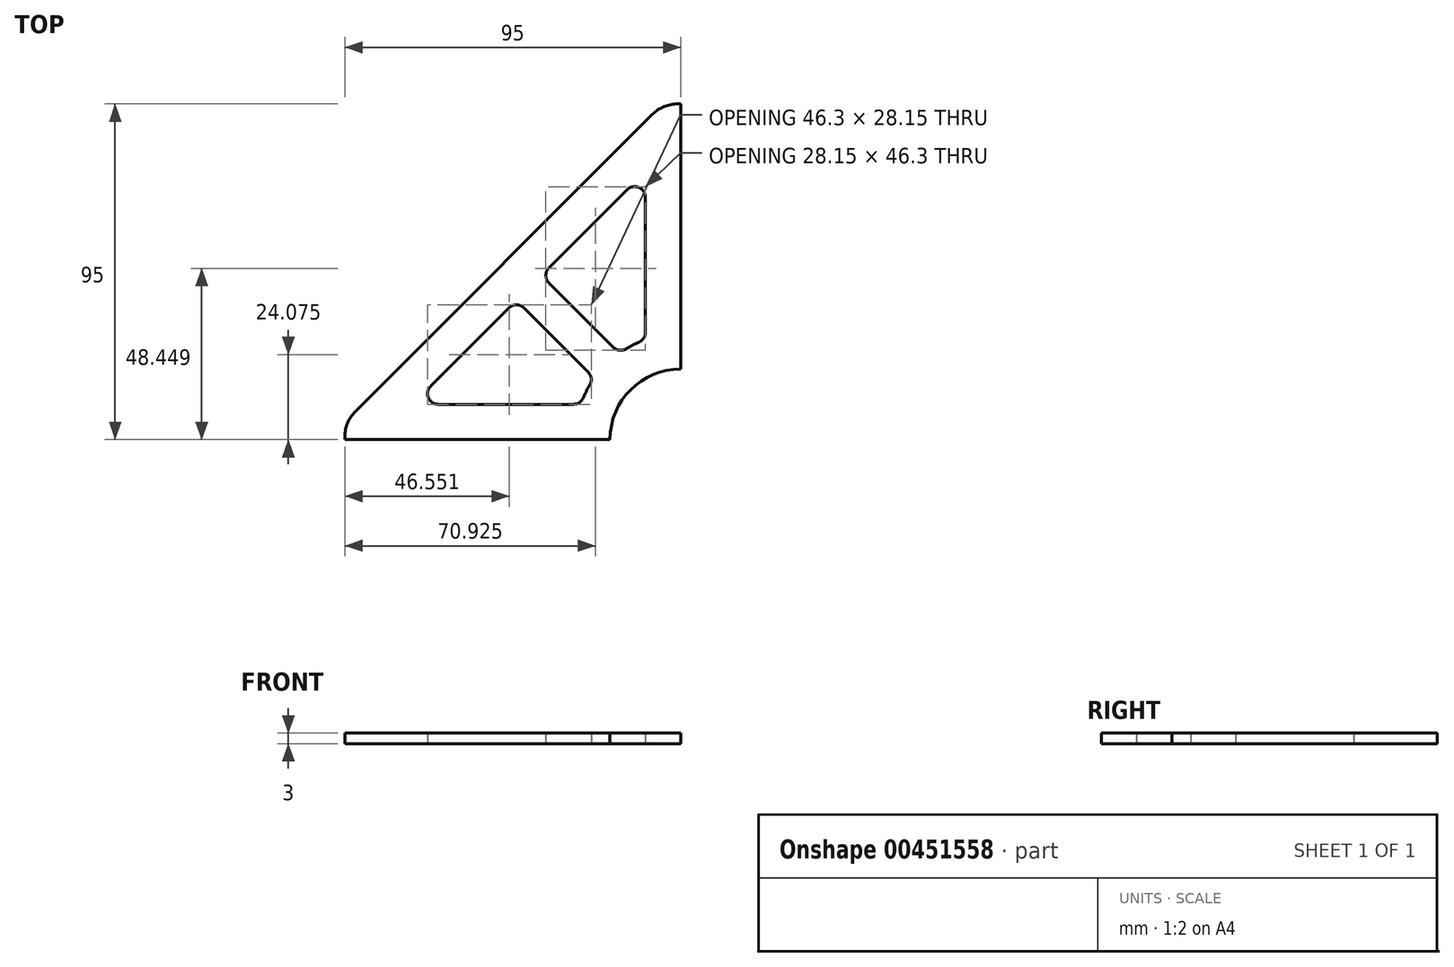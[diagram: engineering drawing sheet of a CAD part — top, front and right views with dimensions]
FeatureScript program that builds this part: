
annotation { "Feature Type Name" : "Feature", "Feature Type Description" : "" }
export const myFeature = defineFeature(function(context is Context, id is Id, definition is map)
    precondition{}
    {
        {
            var Q0;
            Q0=qCreatedBy(makeId("Top.planeOp"),FACE);
            var sketch = newSketch(context, id + "F0", { "sketchPlane" : qUnion([Q0])});
            skLineSegment(sketch, "E0.bottom", {"start": v(0, 0) * mm, "end": v(100, 0) * mm});
            skLineSegment(sketch, "E0.top", {"start": v(0, -100) * mm, "end": v(100, -100) * mm});
            skLineSegment(sketch, "E0.left", {"start": v(0, 0) * mm, "end": v(0, -100) * mm});
            skLineSegment(sketch, "E0.right", {"start": v(100, 0) * mm, "end": v(100, -100) * mm});
            skLineSegment(sketch, "E1", {"start": v(100, 0) * mm, "end": v(0, -100) * mm});
            skLineSegment(sketch, "E2", {"start": v(24.14, -90) * mm, "end": v(53.54, -60.6) * mm});
            skLineSegment(sketch, "E3", {"start": v(60.6, -53.54) * mm, "end": v(90, -24.14) * mm});
            skCircle(sketch, "E4", {"center": v(100, -100) * mm, "radius": 20 * mm});
            skCircle(sketch, "E5", {"center": v(100, -100) * mm, "radius": 30 * mm});
            skLineSegment(sketch, "E6", {"start": v(90, -24.14) * mm, "end": v(90, -71.72) * mm});
            skLineSegment(sketch, "E7", {"start": v(60.6, -53.54) * mm, "end": v(82.62, -75.55) * mm});
            skLineSegment(sketch, "E8", {"start": v(24.14, -90) * mm, "end": v(71.72, -90) * mm});
            skLineSegment(sketch, "E9", {"start": v(53.54, -60.6) * mm, "end": v(75.55, -82.62) * mm});
            skLineSegment(sketch, "E10", {"start": v(100, -100) * mm, "end": v(50, -50) * mm});
            skSolve(sketch);
        }
        {
            var Q0;
            Q0=makeQuery(id+"F0.imprint","IMPRINT",FACE,{"disambiguationData":[TD([[makeQuery(id+"F0.imprint","IMPRINT",EDGE,{"derivedFrom":sQuery(id+"F0.wireOp",EDGE,"E2")}),1.0]])]});
            var Q1;
            {var subQ0=sQuery(id+"F0.wireOp",EDGE,"E5");var subQ6=sQuery(id+"F0.wireOp",EDGE,"E0.top");var subQ9=makeQuery(id+"F0.imprint","INTERSECT",VERTEX,{"derivedFrom":[subQ6,subQ0]});Q1=makeQuery(id+"F0.imprint","IMPRINT",FACE,{"disambiguationData":[TD([[makeQuery(id+"F0.imprint","IMPRINT",EDGE,{"disambiguationData":[TD([[subQ9,-1.0]])],"derivedFrom":subQ6}),1.0]])]});}
            var Q2;
            Q2=makeQuery(id+"F0.imprint","IMPRINT",FACE,{"disambiguationData":[TD([[makeQuery(id+"F0.imprint","IMPRINT",EDGE,{"derivedFrom":sQuery(id+"F0.wireOp",EDGE,"E3")}),1.0]])]});
            var Q3;
            {var subQ0=sQuery(id+"F0.wireOp",EDGE,"E5");var subQ2=sQuery(id+"F0.wireOp",EDGE,"E0.right");var subQ3=makeQuery(id+"F0.imprint","INTERSECT",VERTEX,{"derivedFrom":[subQ2,subQ0]});Q3=makeQuery(id+"F0.imprint","IMPRINT",FACE,{"disambiguationData":[TD([[makeQuery(id+"F0.imprint","IMPRINT",EDGE,{"disambiguationData":[TD([[subQ3,-1.0]])],"derivedFrom":subQ2}),-1.0]])]});}
            extrude(context, id + "F1", {"entities" : qUnion([Q0, Q1, Q2, Q3]), "depth" : 3 * mm});
        }
        {
            var Q0;
            Q0=makeQuery(id+"F1.opExtrude","SWEPT_EDGE",EDGE,{"disambiguationData":[OSD([sQuery(id+"F0.wireOp",EDGE,"E2"),sQuery(id+"F0.wireOp",EDGE,"E8")])]});
            var Q1;
            Q1=makeQuery(id+"F1.opExtrude","SWEPT_EDGE",EDGE,{"disambiguationData":[OSD([sQuery(id+"F0.wireOp",EDGE,"E2"),sQuery(id+"F0.wireOp",EDGE,"E9")])]});
            var Q2;
            Q2=makeQuery(id+"F1.opExtrude","SWEPT_EDGE",EDGE,{"disambiguationData":[OSD([sQuery(id+"F0.wireOp",EDGE,"E5"),sQuery(id+"F0.wireOp",EDGE,"E8")])]});
            var Q3;
            Q3=makeQuery(id+"F1.opExtrude","SWEPT_EDGE",EDGE,{"disambiguationData":[OSD([sQuery(id+"F0.wireOp",EDGE,"E5"),sQuery(id+"F0.wireOp",EDGE,"E9")])]});
            var Q4;
            Q4=makeQuery(id+"F1.opExtrude","SWEPT_EDGE",EDGE,{"disambiguationData":[OSD([sQuery(id+"F0.wireOp",EDGE,"E3"),sQuery(id+"F0.wireOp",EDGE,"E7")])]});
            var Q5;
            Q5=makeQuery(id+"F1.opExtrude","SWEPT_EDGE",EDGE,{"disambiguationData":[OSD([sQuery(id+"F0.wireOp",EDGE,"E5"),sQuery(id+"F0.wireOp",EDGE,"E6")])]});
            var Q6;
            Q6=makeQuery(id+"F1.opExtrude","SWEPT_EDGE",EDGE,{"disambiguationData":[OSD([sQuery(id+"F0.wireOp",EDGE,"E5"),sQuery(id+"F0.wireOp",EDGE,"E7")])]});
            var Q7;
            Q7=makeQuery(id+"F1.opExtrude","SWEPT_EDGE",EDGE,{"disambiguationData":[OSD([sQuery(id+"F0.wireOp",EDGE,"E3"),sQuery(id+"F0.wireOp",EDGE,"E6")])]});
            fillet(context, id + "F2", {"entities" : qUnion([Q0, Q1, Q2, Q3, Q4, Q5, Q6, Q7]), "radius" : 3 * mm, "tangentPropagation" : true, "allowEdgeOverflow" : false});
        }
        {
            var Q0;
            Q0=makeQuery(id+"F1.opExtrude","SWEPT_FACE",FACE,{"disambiguationData":[OSD([sQuery(id+"F0.wireOp",EDGE,"E0.top")])]});
            var sketch = newSketch(context, id + "F3", { "sketchPlane" : qUnion([Q0])});
            skLineSegment(sketch, "E11", {"start": v(5, 0) * mm, "end": v(5, 3) * mm});
            skSolve(sketch);
        }
        {
            var Q0;
            {var subQ0=sQuery(id+"F3.wireOp",EDGE,"E11");Q0=makeQuery(id+"F3.imprint","IMPRINT",FACE,{"disambiguationData":[TD([[makeQuery(id+"F3.imprint","IMPRINT",EDGE,{"derivedFrom":subQ0}),1.0]])]});}
            extrude(context, id + "F4", {"entities" : qUnion([Q0]), "operationType" : NewBodyOperationType.REMOVE, "oppositeDirection" : true, "depth" : 25 * mm});
        }
        {
            var Q0;
            Q0=makeQuery(id+"F1.opExtrude","SWEPT_FACE",FACE,{"disambiguationData":[OSD([sQuery(id+"F0.wireOp",EDGE,"E0.right")])]});
            var sketch = newSketch(context, id + "F5", { "sketchPlane" : qUnion([Q0])});
            skLineSegment(sketch, "E12", {"start": v(-5, 3) * mm, "end": v(-5, 0) * mm});
            skSolve(sketch);
        }
        {
            var Q0;
            {var subQ0=sQuery(id+"F5.wireOp",EDGE,"E12");Q0=makeQuery(id+"F5.imprint","IMPRINT",FACE,{"disambiguationData":[TD([[makeQuery(id+"F5.imprint","IMPRINT",EDGE,{"derivedFrom":subQ0}),1.0]])]});}
            extrude(context, id + "F6", {"entities" : qUnion([Q0]), "operationType" : NewBodyOperationType.REMOVE, "oppositeDirection" : true, "depth" : 25 * mm});
        }
        {
            var Q0;
            Q0=makeQuery(id+"F4.boolean.opBoolean","INTERSECT",EDGE,{"derivedFrom":[makeQuery(id+"F1.opExtrude","SWEPT_FACE",FACE,{"disambiguationData":[OSD([sQuery(id+"F0.wireOp",EDGE,"E1")])]}),makeQuery(id+"F4.opExtrude","SWEPT_FACE",FACE,{"disambiguationData":[OSD([sQuery(id+"F3.wireOp",EDGE,"E11")])]})]});
            var Q1;
            Q1=makeQuery(id+"F6.boolean.opBoolean","INTERSECT",EDGE,{"derivedFrom":[makeQuery(id+"F1.opExtrude","SWEPT_FACE",FACE,{"disambiguationData":[OSD([sQuery(id+"F0.wireOp",EDGE,"E1")])]}),makeQuery(id+"F6.opExtrude","SWEPT_FACE",FACE,{"disambiguationData":[OSD([sQuery(id+"F5.wireOp",EDGE,"E12")])]})]});
            fillet(context, id + "F7", {"entities" : qUnion([Q0, Q1]), "radius" : 10 * mm, "tangentPropagation" : true, "allowEdgeOverflow" : false});
        }
    });
